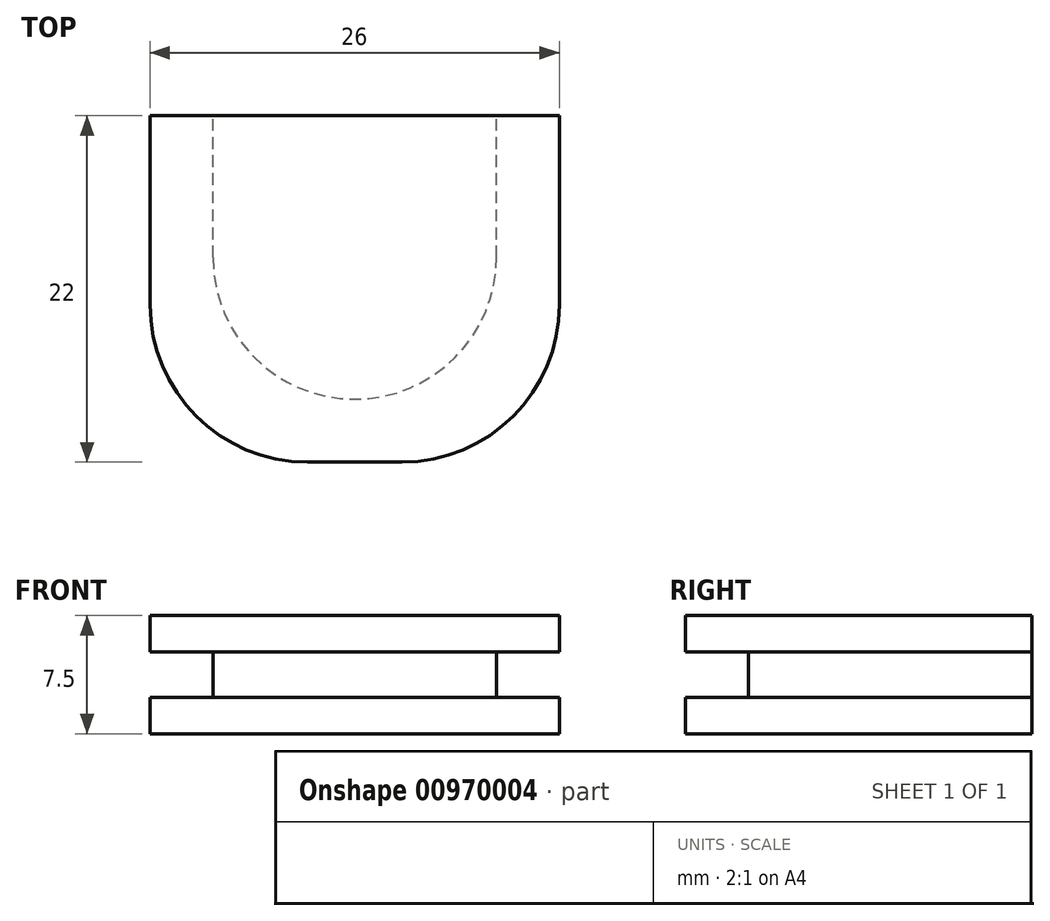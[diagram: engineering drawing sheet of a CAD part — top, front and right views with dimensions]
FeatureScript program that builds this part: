
annotation { "Feature Type Name" : "Feature", "Feature Type Description" : "" }
export const myFeature = defineFeature(function(context is Context, id is Id, definition is map)
    precondition{}
    {
        {
            var Q0;
            Q0=qCreatedBy(makeId("Top.planeOp"),FACE);
            var sketch = newSketch(context, id + "F0", { "sketchPlane" : qUnion([Q0])});
            skLineSegment(sketch, "E0.bottom", {"start": v(9, -9) * mm, "end": v(-9, -9) * mm});
            skLineSegment(sketch, "E0.top", {"start": v(9, 9) * mm, "end": v(-9, 9) * mm});
            skLineSegment(sketch, "E0.left", {"start": v(9, -9) * mm, "end": v(9, 9) * mm});
            skLineSegment(sketch, "E0.right", {"start": v(-9, -9) * mm, "end": v(-9, 9) * mm});
            skPoint(sketch, "E0.middle", {"position": v(0, 0) * mm});
            skSolve(sketch);
        }
        {
            var Q0;
            Q0=qCreatedBy(makeId("Top.planeOp"),FACE);
            var sketch = newSketch(context, id + "F1", { "sketchPlane" : qUnion([Q0])});
            skLineSegment(sketch, "E1.0", {"start": v(-13, -13) * mm, "end": v(-13, 9) * mm});
            skLineSegment(sketch, "E2.0", {"start": v(13, -13) * mm, "end": v(-13, -13) * mm});
            skLineSegment(sketch, "E3.0", {"start": v(13, -13) * mm, "end": v(13, 9) * mm});
            skLineSegment(sketch, "E4", {"start": v(-13, 9) * mm, "end": v(13, 9) * mm});
            skSolve(sketch);
        }
        {
            var Q0;
            Q0 = qSketchRegion(id + "F1", true);
            extrude(context, id + "F2", {"entities" : qUnion([Q0]), "depth" : 2.3 * mm, "offsetDistance" : 25 * mm});
        }
        {
            var Q0;
            Q0 = qSketchRegion(id + "F1", true);
            extrude(context, id + "F3", {"entities" : qUnion([Q0]), "depth" : 7.5 * mm, "offsetDistance" : 25 * mm, "hasSecondDirection" : true, "secondDirectionOppositeDirection" : false, "secondDirectionDepth" : 5.2 * mm});
        }
        {
            var Q0;
            Q0 = qSketchRegion(id + "F0", true);
            extrude(context, id + "F4", {"entities" : qUnion([Q0]), "depth" : 5.2 * mm, "offsetDistance" : 25 * mm, "hasSecondDirection" : true, "secondDirectionOppositeDirection" : false, "secondDirectionDepth" : 2.3 * mm});
        }
        {
            var Q0;
            Q0=makeQuery(id+"F4.opExtrude","SWEPT_EDGE",EDGE,{"disambiguationData":[OSD([sQuery(id+"F0.wireOp",EDGE,"E0.bottom"),sQuery(id+"F0.wireOp",EDGE,"E0.right")])]});
            var Q1;
            Q1=makeQuery(id+"F4.opExtrude","SWEPT_EDGE",EDGE,{"disambiguationData":[OSD([sQuery(id+"F0.wireOp",EDGE,"E0.bottom"),sQuery(id+"F0.wireOp",EDGE,"E0.left")])]});
            fillet(context, id + "F5", {"entities" : qUnion([Q0, Q1]), "radius" : 9 * mm, "tangentPropagation" : true, "allowEdgeOverflow" : false});
        }
        {
            var Q0;
            Q0=makeQuery(id+"F3.opExtrude","SWEPT_EDGE",EDGE,{"disambiguationData":[OSD([sQuery(id+"F1.wireOp",EDGE,"E1.0"),sQuery(id+"F1.wireOp",EDGE,"E2.0")])]});
            var Q1;
            Q1=makeQuery(id+"F3.opExtrude","SWEPT_EDGE",EDGE,{"disambiguationData":[OSD([sQuery(id+"F1.wireOp",EDGE,"E2.0"),sQuery(id+"F1.wireOp",EDGE,"E3.0")])]});
            var Q2;
            Q2=makeQuery(id+"F2.opExtrude","SWEPT_EDGE",EDGE,{"disambiguationData":[OSD([sQuery(id+"F1.wireOp",EDGE,"E2.0"),sQuery(id+"F1.wireOp",EDGE,"E3.0")])]});
            var Q3;
            Q3=makeQuery(id+"F2.opExtrude","SWEPT_EDGE",EDGE,{"disambiguationData":[OSD([sQuery(id+"F1.wireOp",EDGE,"E1.0"),sQuery(id+"F1.wireOp",EDGE,"E2.0")])]});
            fillet(context, id + "F6", {"entities" : qUnion([Q0, Q1, Q2, Q3]), "radius" : 10 * mm, "tangentPropagation" : true, "allowEdgeOverflow" : false});
        }
    });
